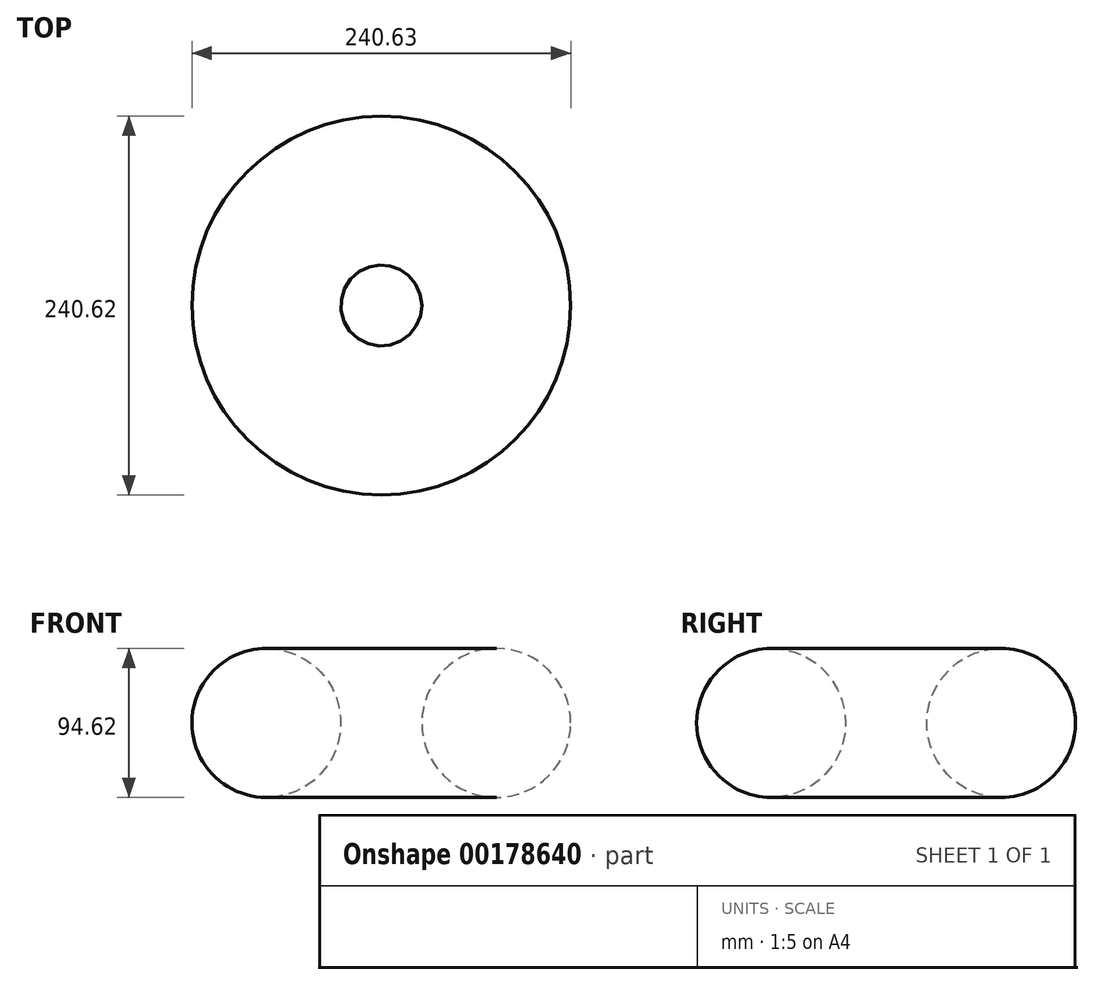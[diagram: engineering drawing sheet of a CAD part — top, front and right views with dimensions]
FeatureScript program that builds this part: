
annotation { "Feature Type Name" : "Feature", "Feature Type Description" : "" }
export const myFeature = defineFeature(function(context is Context, id is Id, definition is map)
    precondition{}
    {
        {
            var Q0;
            Q0=qCreatedBy(makeId("Front.planeOp"),FACE);
            var sketch = newSketch(context, id + "F0", { "sketchPlane" : qUnion([Q0])});
            skLineSegment(sketch, "E0", {"start": v(-46.34, 56.17) * mm, "end": v(-46.34, -55.28) * mm});
            skCircle(sketch, "E1", {"center": v(26.67, 0) * mm, "radius": 47.3 * mm});
            skSolve(sketch);
        }
        {
            var Q0;
            Q0=makeQuery(id+"F0.imprint","IMPRINT",FACE,{"disambiguationData":[TD([[makeQuery(id+"F0.imprint","IMPRINT",EDGE,{"derivedFrom":sQuery(id+"F0.wireOp",EDGE,"E1")}),1.0]])]});
            var Q1;
            Q1=sQuery(id+"F0.wireOp",EDGE,"E0");
            revolve(context, id + "F1", {"entities" : qUnion([Q0]), "axis" : qUnion([Q1]), "revolveType" : RevolveType.FULL});
        }
    });
